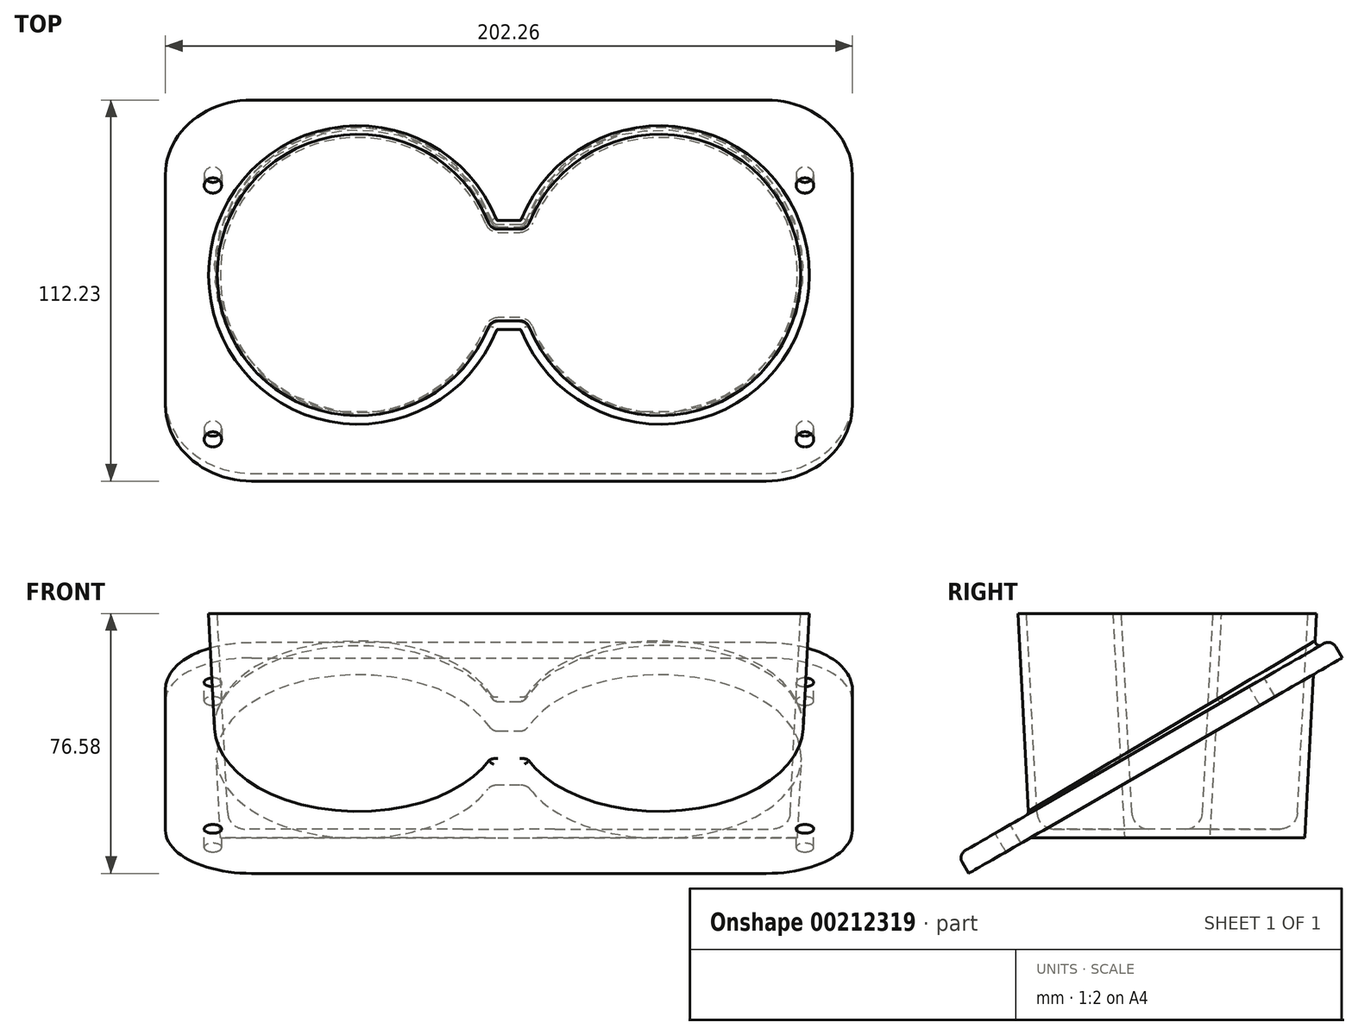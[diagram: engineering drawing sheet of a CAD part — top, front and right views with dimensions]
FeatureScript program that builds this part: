
annotation { "Feature Type Name" : "Feature", "Feature Type Description" : "" }
export const myFeature = defineFeature(function(context is Context, id is Id, definition is map)
    precondition{}
    {
        {
            var Q0;
            Q0=qCreatedBy(makeId("Top.planeOp"),FACE);
            var sketch = newSketch(context, id + "F0", { "sketchPlane" : qUnion([Q0])});
            skLineSegment(sketch, "E0", {"start": v(-44.46, 0) * mm, "end": v(44.46, 0) * mm, "construction": true});
            skArc(sketch, "E1", {"start": v(9.09, -14.15) * mm, "mid": v(82.56, 0) * mm, "end": v(9.09, 14.15) * mm});
            skArc(sketch, "E2", {"start": v(-9.09, 14.15) * mm, "mid": v(-82.56, 0) * mm, "end": v(-9.09, -14.15) * mm});
            skLineSegment(sketch, "E3", {"start": v(-3.2, 10.16) * mm, "end": v(3.2, 10.16) * mm});
            skLineSegment(sketch, "E4", {"start": v(-3.2, -10.16) * mm, "end": v(3.2, -10.16) * mm});
            skPoint(sketch, "E5.visualSharp", {"position": v(-7.74, 10.16) * mm});
            skArc(sketch, "E5.filletArc", {"start": v(-9.09, 14.15) * mm, "mid": v(-6.75, 11.25) * mm, "end": v(-3.2, 10.16) * mm});
            skPoint(sketch, "E6.visualSharp", {"position": v(7.74, 10.16) * mm});
            skArc(sketch, "E6.filletArc", {"start": v(3.2, 10.16) * mm, "mid": v(6.75, 11.25) * mm, "end": v(9.09, 14.15) * mm});
            skPoint(sketch, "E7.visualSharp", {"position": v(7.74, -10.16) * mm});
            skArc(sketch, "E7.filletArc", {"start": v(9.09, -14.15) * mm, "mid": v(6.75, -11.25) * mm, "end": v(3.2, -10.16) * mm});
            skPoint(sketch, "E8.visualSharp", {"position": v(-7.74, -10.16) * mm});
            skArc(sketch, "E8.filletArc", {"start": v(-3.2, -10.16) * mm, "mid": v(-6.75, -11.25) * mm, "end": v(-9.09, -14.15) * mm});
            skSolve(sketch);
        }
        {
            var Q0;
            Q0=makeQuery(id+"F0.imprint","IMPRINT",FACE,{"disambiguationData":[TD([[makeQuery(id+"F0.imprint","IMPRINT",EDGE,{"derivedFrom":sQuery(id+"F0.wireOp",EDGE,"E1")}),1.0]])]});
            extrude(context, id + "F1", {"entities" : qUnion([Q0]), "depth" : 63.5 * mm, "hasDraft" : true, "draftAngle" : 3 * degree});
        }
        {
            var Q0;
            Q0=makeQuery(id+"F1.opExtrude","CAP_FACE",FACE,{"disambiguationData":[OSD([sQuery(id+"F0.wireOp",EDGE,"E1"),sQuery(id+"F0.wireOp",EDGE,"E2"),sQuery(id+"F0.wireOp",EDGE,"E3"),sQuery(id+"F0.wireOp",EDGE,"E4"),sQuery(id+"F0.wireOp",EDGE,"E5.filletArc"),sQuery(id+"F0.wireOp",EDGE,"E6.filletArc"),sQuery(id+"F0.wireOp",EDGE,"E7.filletArc"),sQuery(id+"F0.wireOp",EDGE,"E8.filletArc")])],"isStart":false});
            shell(context, id + "F2", {"entities" : qUnion([Q0]), "thickness" : 2.54 * mm, "oppositeDirection" : true});
        }
        {
            var Q0;
            Q0=qCreatedBy(makeId("Right.planeOp"),FACE);
            var sketch = newSketch(context, id + "F3", { "sketchPlane" : qUnion([Q0])});
            skLineSegment(sketch, "E9", {"start": v(0, 0) * mm, "end": v(0, -12.15) * mm});
            skLineSegment(sketch, "E10", {"start": v(0, -2.54) * mm, "end": v(-41.91, -2.54) * mm, "construction": true});
            skLineSegment(sketch, "E11", {"start": v(-41.91, -2.54) * mm, "end": v(-41.91, 3.8) * mm, "construction": true});
            skLineSegment(sketch, "E12", {"start": v(-41.91, 3.8) * mm, "end": v(68.08, 67.31) * mm});
            skSolve(sketch);
        }
        {
            var Q0;
            Q0=sQuery(id+"F3.wireOp",EDGE,"E12");
            cPlane(context, id + "F4", {"entities" : qUnion([Q0]), "cplaneType" : CPlaneType.LINE_ANGLE, "offset" : 25.4 * mm, "angle" : 0 * degree, "width" : 152.4 * mm, "height" : 152.4 * mm});
        }
        {
            var Q0;
            Q0=qCreatedBy(id+"F4.planeOp",FACE);
            var sketch = newSketch(context, id + "F5", { "sketchPlane" : qUnion([Q0])});
            skLineSegment(sketch, "E13.bottom", {"start": v(-101.13, 69.83) * mm, "end": v(101.13, 69.83) * mm});
            skLineSegment(sketch, "E13.top", {"start": v(-101.13, -57.17) * mm, "end": v(101.13, -57.17) * mm});
            skLineSegment(sketch, "E13.left", {"start": v(-101.13, 69.83) * mm, "end": v(-101.13, -57.17) * mm});
            skLineSegment(sketch, "E13.right", {"start": v(101.13, 69.83) * mm, "end": v(101.13, -57.17) * mm});
            skLineSegment(sketch, "E14", {"start": v(50.89, 69.83) * mm, "end": v(-122.99, 69.83) * mm, "construction": true});
            skLineSegment(sketch, "E15", {"start": v(-122.99, 69.83) * mm, "end": v(156.1, 69.83) * mm, "construction": true});
            skSolve(sketch);
        }
        {
            var Q0;
            Q0=makeQuery(id+"F5.imprint","IMPRINT",FACE,{"disambiguationData":[TD([[makeQuery(id+"F5.imprint","IMPRINT",EDGE,{"derivedFrom":sQuery(id+"F5.wireOp",EDGE,"E13.bottom")}),-1.0]])]});
            extrude(context, id + "F6", {"entities" : qUnion([Q0]), "operationType" : NewBodyOperationType.ADD, "oppositeDirection" : true, "depth" : 6.35 * mm});
        }
        {
            var Q0;
            Q0=qCreatedBy(makeId("Top.planeOp"),FACE);
            var sketch = newSketch(context, id + "F7", { "sketchPlane" : qUnion([Q0])});
            skLineSegment(sketch, "E16", {"start": v(-44.46, 0) * mm, "end": v(44.46, 0) * mm, "construction": true});
            skArc(sketch, "E17", {"start": v(9.09, -14.15) * mm, "mid": v(82.56, 0) * mm, "end": v(9.09, 14.15) * mm});
            skArc(sketch, "E18", {"start": v(-9.09, 14.15) * mm, "mid": v(-82.56, 0) * mm, "end": v(-9.09, -14.15) * mm});
            skLineSegment(sketch, "E19", {"start": v(-3.2, 10.16) * mm, "end": v(3.2, 10.16) * mm});
            skLineSegment(sketch, "E20", {"start": v(-3.2, -10.16) * mm, "end": v(3.2, -10.16) * mm});
            skPoint(sketch, "E21.visualSharp", {"position": v(-7.74, 10.16) * mm});
            skArc(sketch, "E21.filletArc", {"start": v(-9.09, 14.15) * mm, "mid": v(-6.75, 11.25) * mm, "end": v(-3.2, 10.16) * mm});
            skPoint(sketch, "E22.visualSharp", {"position": v(7.74, 10.16) * mm});
            skArc(sketch, "E22.filletArc", {"start": v(3.2, 10.16) * mm, "mid": v(6.75, 11.25) * mm, "end": v(9.09, 14.15) * mm});
            skPoint(sketch, "E23.visualSharp", {"position": v(7.74, -10.16) * mm});
            skArc(sketch, "E23.filletArc", {"start": v(9.09, -14.15) * mm, "mid": v(6.75, -11.25) * mm, "end": v(3.2, -10.16) * mm});
            skPoint(sketch, "E24.visualSharp", {"position": v(-7.74, -10.16) * mm});
            skArc(sketch, "E24.filletArc", {"start": v(-3.2, -10.16) * mm, "mid": v(-6.75, -11.25) * mm, "end": v(-9.09, -14.15) * mm});
            skSolve(sketch);
        }
        {
            var Q0;
            Q0 = qSketchRegion(id + "F7", true);
            extrude(context, id + "F8", {"entities" : qUnion([Q0]), "operationType" : NewBodyOperationType.REMOVE, "depth" : 76.2 * mm, "hasDraft" : true, "draftAngle" : 3 * degree});
        }
        {
            var Q0;
            Q0=makeQuery(id+"F6.opExtrude","CAP_EDGE",EDGE,{"disambiguationData":[OSD([sQuery(id+"F5.wireOp",EDGE,"E13.bottom")])],"isStart":true});
            var Q1;
            Q1=makeQuery(id+"F6.opExtrude","CAP_EDGE",EDGE,{"disambiguationData":[OSD([sQuery(id+"F5.wireOp",EDGE,"E13.left")])],"isStart":true});
            var Q2;
            Q2=makeQuery(id+"F6.opExtrude","CAP_EDGE",EDGE,{"disambiguationData":[OSD([sQuery(id+"F5.wireOp",EDGE,"E13.top")])],"isStart":true});
            var Q3;
            Q3=makeQuery(id+"F6.opExtrude","CAP_EDGE",EDGE,{"disambiguationData":[OSD([sQuery(id+"F5.wireOp",EDGE,"E13.right")])],"isStart":true});
            fillet(context, id + "F9", {"entities" : qUnion([Q0, Q1, Q2, Q3]), "radius" : 2.54 * mm, "tangentPropagation" : true, "allowEdgeOverflow" : false});
        }
        {
            var Q0;
            Q0=makeQuery(id+"F6.opExtrude","SWEPT_EDGE",EDGE,{"disambiguationData":[OSD([sQuery(id+"F5.wireOp",EDGE,"E13.top"),sQuery(id+"F5.wireOp",EDGE,"E13.left")])]});
            var Q1;
            Q1=makeQuery(id+"F6.opExtrude","SWEPT_EDGE",EDGE,{"disambiguationData":[OSD([sQuery(id+"F5.wireOp",EDGE,"E13.top"),sQuery(id+"F5.wireOp",EDGE,"E13.right")])]});
            var Q2;
            Q2=makeQuery(id+"F6.opExtrude","SWEPT_EDGE",EDGE,{"disambiguationData":[OSD([sQuery(id+"F5.wireOp",EDGE,"E13.bottom"),sQuery(id+"F5.wireOp",EDGE,"E13.left")])]});
            var Q3;
            Q3=makeQuery(id+"F6.opExtrude","SWEPT_EDGE",EDGE,{"disambiguationData":[OSD([sQuery(id+"F5.wireOp",EDGE,"E13.bottom"),sQuery(id+"F5.wireOp",EDGE,"E13.right")])]});
            fillet(context, id + "F10", {"entities" : qUnion([Q0, Q1, Q2, Q3]), "radius" : 25.4 * mm, "tangentPropagation" : true, "allowEdgeOverflow" : false});
        }
        {
            var Q0;
            {var subQ0=sQuery(id+"F5.wireOp",EDGE,"E13.top");var subQ1=sQuery(id+"F5.wireOp",EDGE,"E13.bottom");var subQ2=sQuery(id+"F5.wireOp",EDGE,"E13.left");var subQ3=sQuery(id+"F5.wireOp",EDGE,"E13.right");Q0=makeQuery(id+"F6.boolean.opBoolean","SPLIT",FACE,{"disambiguationData":[TD([makeQuery(id+"F1.opExtrude","SWEPT_FACE",FACE,{"disambiguationData":[OSD([sQuery(id+"F0.wireOp",EDGE,"E1")])]})])],"derivedFrom":makeQuery(id+"F6.opExtrude","CAP_FACE",FACE,{"disambiguationData":[OSD([subQ1,subQ0,subQ2,subQ3])],"isStart":true})});}
            var sketch = newSketch(context, id + "F11", { "sketchPlane" : qUnion([Q0])});
            skLineSegment(sketch, "E25", {"start": v(-87.16, -41.93) * mm, "end": v(87.16, -41.93) * mm, "construction": true});
            skLineSegment(sketch, "E26", {"start": v(87.16, -41.93) * mm, "end": v(87.16, 44.43) * mm, "construction": true});
            skLineSegment(sketch, "E27", {"start": v(87.16, 44.43) * mm, "end": v(-87.16, 44.43) * mm, "construction": true});
            skLineSegment(sketch, "E28", {"start": v(-87.16, -41.93) * mm, "end": v(-87.16, 44.43) * mm, "construction": true});
            skSolve(sketch);
        }
        {
            var Q0;
            Q0=sQuery(id+"F11.wireOp",VERTEX,"E26.start");
            var Q1;
            Q1=sQuery(id+"F11.wireOp",VERTEX,"E26.end");
            var Q2;
            Q2=sQuery(id+"F11.wireOp",VERTEX,"E28.start");
            var Q3;
            Q3=sQuery(id+"F11.wireOp",VERTEX,"E28.end");
            var Q4;
            Q4=makeQuery(id+"F1.opExtrude","SWEPT_BODY",BODY,{"disambiguationData":[OSD([sQuery(id+"F0.wireOp",EDGE,"E1"),sQuery(id+"F0.wireOp",EDGE,"E2"),sQuery(id+"F0.wireOp",EDGE,"E3"),sQuery(id+"F0.wireOp",EDGE,"E4"),sQuery(id+"F0.wireOp",EDGE,"E5.filletArc"),sQuery(id+"F0.wireOp",EDGE,"E6.filletArc"),sQuery(id+"F0.wireOp",EDGE,"E7.filletArc"),sQuery(id+"F0.wireOp",EDGE,"E8.filletArc")])]});
            hole(context, id + "F12", {"style" : HoleStyle.SIMPLE, "endStyle" : HoleEndStyle.BLIND, "holeDiameter" : 5.16 * mm, "holeDepth" : 17.78 * mm, "startFromSketch" : true, "locations" : qUnion([Q0, Q1, Q2, Q3]), "scope" : qUnion([Q4])});
        }
        {
            var Q0;
            {var subQ0=sQuery(id+"F0.wireOp",EDGE,"E8.filletArc");var subQ1=sQuery(id+"F0.wireOp",EDGE,"E5.filletArc");var subQ2=sQuery(id+"F0.wireOp",EDGE,"E2");var subQ6=makeQuery(id+"F2.opShell","OFFSET_EDGE",EDGE,{"disambiguationData":[OSD([subQ2]),TDD([makeQuery(id+"F1.opExtrude","CAP_EDGE",EDGE,{"disambiguationData":[OSD([subQ2])],"isStart":true})])]});Q0=makeQuery(id+"F8.boolean.opBoolean","MERGE",EDGE,{"derivedFrom":[makeQuery(id+"F6.boolean.opBoolean","SPLIT",EDGE,{"disambiguationData":[TD([makeQuery(id+"F2.opShell","OFFSET_FACE",FACE,{"disambiguationData":[OSD([subQ1])]})])],"derivedFrom":subQ6}),makeQuery(id+"F6.boolean.opBoolean","SPLIT",EDGE,{"disambiguationData":[TD([makeQuery(id+"F2.opShell","OFFSET_FACE",FACE,{"disambiguationData":[OSD([subQ0])]})])],"derivedFrom":subQ6}),makeQuery(id+"F8.opExtrude","CAP_EDGE",EDGE,{"disambiguationData":[OSD([sQuery(id+"F7.wireOp",EDGE,"E18")])],"isStart":true})]});}
            fillet(context, id + "F13", {"entities" : qUnion([Q0]), "radius" : 5.08 * mm, "tangentPropagation" : true, "allowEdgeOverflow" : false});
        }
        {
            var Q0;
            Q0=makeQuery(id+"F6.boolean.opBoolean","INTERSECT",EDGE,{"derivedFrom":[makeQuery(id+"F1.opExtrude","SWEPT_FACE",FACE,{"disambiguationData":[OSD([sQuery(id+"F0.wireOp",EDGE,"E1")])]}),makeQuery(id+"F6.opExtrude","CAP_FACE",FACE,{"disambiguationData":[OSD([sQuery(id+"F5.wireOp",EDGE,"E13.bottom"),sQuery(id+"F5.wireOp",EDGE,"E13.top"),sQuery(id+"F5.wireOp",EDGE,"E13.left"),sQuery(id+"F5.wireOp",EDGE,"E13.right")])],"isStart":true})]});
            fillet(context, id + "F14", {"entities" : qUnion([Q0]), "radius" : 1.27 * mm, "tangentPropagation" : true, "allowEdgeOverflow" : false});
        }
    });
